# Revit family: Tempo-X161-Wallwasher
name_source: partatom
category: Lighting Fixtures
revit_build: Autodesk Revit MEP 2014 (Build: 20130308_1515(x64)
units: mm (PartAtom-declared; Revit-internal decimal feet)

## types (2) — shared parameters
Aperture (mm) = 120
CRI = 80
Color Filter = 16777215
Dimming Lamp Color Temperature Shift = <None>
Lamp = LED
Luminous flux of luminaire (lm) = 2000
Manufacturer = Designed Architectural Lighting
Type Comments = Recessed

## per-type parameters (varying)
| type | Apparent Load | Colour temperature (K) | Cut Out (mm) | Description | Height (mm) | Model | O/A Diameter (mm) | Photometric Web File | Tilt Angle | Type | Wattage Comments |
| Type S-BDL | 23 VA | 3000 | 156 | Recessed low brightness LED trimless downlighter / double washer | 188 | A4000/S-BDL | 140.50 | generic | 60.00° | A4000/S-BDL | 23 |
| Tempo X161 Wallwasher | 20 VA | 2700, 3000, 3500, 4000K | 147 | Recessed LED Wallwasher | 105 | C7901 | 161 | C7901-XTM.ies | 90.00° | C7901 | 19.5 |

## geometry (parser evidence)
native form markers: Sweep x3
no freeform markers — native parametric forms only
